FCSTD DOCUMENT  (FreeCAD 0.20R0.20)
Label: 001
License: All rights reserved
LicenseURL: http://en.wikipedia.org/wiki/All_rights_reserved
objects: Sketcher::SketchObject×1
note: 1 computed .brp shape members not serialized (recipe doc carries the construction recipe); baked Part::Feature solids carry a one-line shape summary decoded from their .brp

FEATURE [Sketcher::SketchObject] Sketch
  FullyConstrained = true
  sketch-geometry (19):
    g0: LineSegment StartX=0 StartY=0 StartZ=0 EndX=80 EndY=0 EndZ=0
    g1: LineSegment StartX=0 StartY=0 StartZ=0 EndX=0 EndY=80 EndZ=0
    g2: LineSegment StartX=0 StartY=80 StartZ=0 EndX=3.5 EndY=80 EndZ=0
    g3: LineSegment StartX=3.5 StartY=80 StartZ=0 EndX=6.5 EndY=80 EndZ=0
    g4: LineSegment StartX=6.5 StartY=80 StartZ=0 EndX=13.5 EndY=80 EndZ=0
    g5: LineSegment StartX=13.5 StartY=80 StartZ=0 EndX=16.5 EndY=80 EndZ=0
    g6: LineSegment StartX=16.5 StartY=80 StartZ=0 EndX=23.5 EndY=80 EndZ=0
    g7: LineSegment StartX=23.5 StartY=80 StartZ=0 EndX=26.5 EndY=80 EndZ=0
    g8: LineSegment StartX=26.5 StartY=80 StartZ=0 EndX=33.5 EndY=80 EndZ=0
    g9: LineSegment StartX=33.5 StartY=80 StartZ=0 EndX=36.5 EndY=80 EndZ=0
    g10: LineSegment StartX=36.5 StartY=80 StartZ=0 EndX=43.5 EndY=80 EndZ=0
    g11: LineSegment StartX=43.5 StartY=80 StartZ=0 EndX=46.5 EndY=80 EndZ=0
    g12: LineSegment StartX=46.5 StartY=80 StartZ=0 EndX=53.5 EndY=80 EndZ=0
    g13: LineSegment StartX=56.5 StartY=80 StartZ=0 EndX=63.5 EndY=80 EndZ=0
    g14: LineSegment StartX=53.5 StartY=80 StartZ=0 EndX=56.5 EndY=80 EndZ=0
    g15: LineSegment StartX=63.5 StartY=80 StartZ=0 EndX=66.5 EndY=80 EndZ=0
    g16: LineSegment StartX=66.5 StartY=80 StartZ=0 EndX=73.5 EndY=80 EndZ=0
    g17: LineSegment StartX=73.5 StartY=80 StartZ=0 EndX=76.5 EndY=80 EndZ=0
    g18: LineSegment StartX=76.5 StartY=80 StartZ=0 EndX=80 EndY=80 EndZ=0
  constraints (57):
    c: Coincident(g0,g-1)
    c: Horizontal(g0)
    c: Distance(g0) = 80
    c: Coincident(g1,g0)
    c: Vertical(g1)
    c: Coincident(g2,g1)
    c: Horizontal(g2)
    c: Distance(g2) = 3.5
    c: Coincident(g3,g2)
    c: Horizontal(g3)
    c: Distance(g3) = 3
    c: Block(g1)
    c: Coincident(g4,g3)
    c: Horizontal(g4)
    c: Coincident(g5,g4)
    c: Horizontal(g5)
    c: Coincident(g6,g5)
    c: Horizontal(g6)
    c: Coincident(g7,g6)
    c: Horizontal(g7)
    c: Coincident(g8,g7)
    c: Horizontal(g8)
    c: Distance(g4) = 7
    c: Distance(g5) = 3
    c: Distance(g6) = 7
    c: Distance(g7) = 3
    c: Distance(g8) = 7
    c: Coincident(g9,g8)
    c: Horizontal(g9)
    c: Coincident(g10,g9)
    c: Horizontal(g10)
    c: Coincident(g11,g10)
    c: Horizontal(g11)
    c: Coincident(g12,g11)
    c: Horizontal(g12)
    c: Horizontal(g13)
    c: Distance(g9) = 3
    c: Distance(g10) = 7
    c: Distance(g11) = 3
    c: Distance(g12) = 7
    c: Coincident(g14,g12)
    c: Coincident(g14,g13)
    c: Horizontal(g14)
    c: Distance(g14) = 3
    c: Distance(g13) = 7
    c: Coincident(g15,g13)
    c: Horizontal(g15)
    c: Coincident(g16,g15)
    c: Coincident(g17,g16)
    c: Horizontal(g17)
    c: Horizontal(g16)
    c: Distance(g15) = 3
    c: Distance(g16) = 7
    c: Distance(g17) = 3
    c: Coincident(g18,g17)
    c: Horizontal(g18)
    c: Distance(g18) = 3.5
